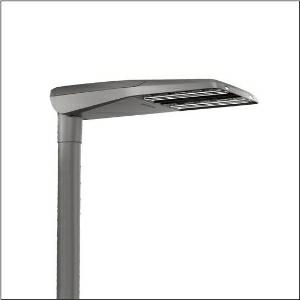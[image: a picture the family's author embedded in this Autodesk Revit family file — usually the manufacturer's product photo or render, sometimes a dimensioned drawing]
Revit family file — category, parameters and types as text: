
# Revit family: streetlight_sl_11_iq_midi___st1_2p1_0_5xc3g41e08me_f4ca
name_source: partatom
category: Lighting Fixtures
units: mm (PartAtom-declared; Revit-internal decimal feet)

## family parameters
Cut with Voids When Loaded = No
Host = Face
Light Source = No
Part Type = Normal
Room Calculation Point = No
Round Connector Dimension = Use Diameter
Shared = No

## types (1)
- --- (1 x LED, 18520 lm, 124.7 W, 4000K)
    Apparent Load = 125 VA
    CIE Flux Codes = 31 68 95 100 100
    Color Rendering = 70
    Color Temperature = 4000K
    Default Elevation = 1800 mm
    Description = Streetlight SL 11 iQ midi, mast luminaire, primary light control with 3 zone facetted reflector, of plastic, silver coated, highly specular, primary optical cover: cover, of PMMA, transparent, light distribution: ST1.2P1.0, light emission: direct distribution, primary light characteristic: asymmetric, installation type: post-top, side-entry, LED, High Power LED, rated luminous flux: 18.520lm, luminous efficacy: 149lm/W, light colour: 740, colour temperature: 4000K, control: optimised constant luminous flux control (CLO 2.0), Desk-Remote (wireless, voltage-free reading and setting of iQ features in the workshop via application-optimized NFC function/RFID function), Light-Fading, Smart-Wire, Night-Set, Lumen-Switch, Temp-Guard, Auto-Match, with cable H07RN-F 5x 1.5mm², mains connection: 220..240V, AC, 50/60Hz, connection cable pre-assembled, cable length: 12,5m, start of lifetime: 125W, end of lifetime: 132W, reduction: 57W, luminaire housing, of diecast aluminium, powder-coated, Siteco® metallic grey (DB 702S), length: 780mm, width: 376mm, height: 118mm, spigot size: 60/76mm (post-top) and 42/60/76mm (side-entry), mast flange for spigot size: 42mm: 5XC10008XM4, 60mm: 5XC10008XM2, 76/60mm: 5XC10108XM1, equipment: Power, protection rating (complete): IP66, insulation class (complete): insulation class II (safety insulation), certification: CE, ENEC, VDE, impact resistance: IK09, permissible operating ambient temperature for outdoor applications: -25..+50°C, standard-compliant lighting for roads and squares, packaging unit: 1 piece

Light Distribution: ST1.2P1.0
    Height = 118 mm
    Lamp = 1 x LED
    Lamp Light Flux = 18520 lm
    Lamp Power = 124.7 W
    Lamp count = 1
    Length = 780 mm
    Luminous efficacy = 149 lm/W
    Manufacturer = Siteco
    ModVariant = No
    Model = 5XC3G41E08ME
    Number of Poles = 1
    OnlyDefault = Yes
    Power Factor = 1
    Product Name = Streetlight SL 11 iQ midi | ST1.2P1.0
    Product group = mast luminaire | pylon top
    ProductGroupID = 6100
    Protection Class = Protection class II
    Protection Degree = IP 66
    RLX_Detail_Level = 1
    RlxData = <blob elided: 70369 chars, md5=b7f841bb>
    Socket = socket
    Standby Power = 0 W
    System Light Flux = 18520 lm
    System Power = 125 W
    Type Comments = factory setting: luminous flux: 100 % | dim-lin: 254 | 557 mA
    Type Image = l_1005960.jpg
    URL = http://relux.com
    VarID = @adj_116247
    Voltage = 0 V
    Weight = 0.00 kg
    Width = 376 mm

## geometry (parser evidence)
native form markers: Blend x4, Sweep x11
no freeform markers — native parametric forms only
